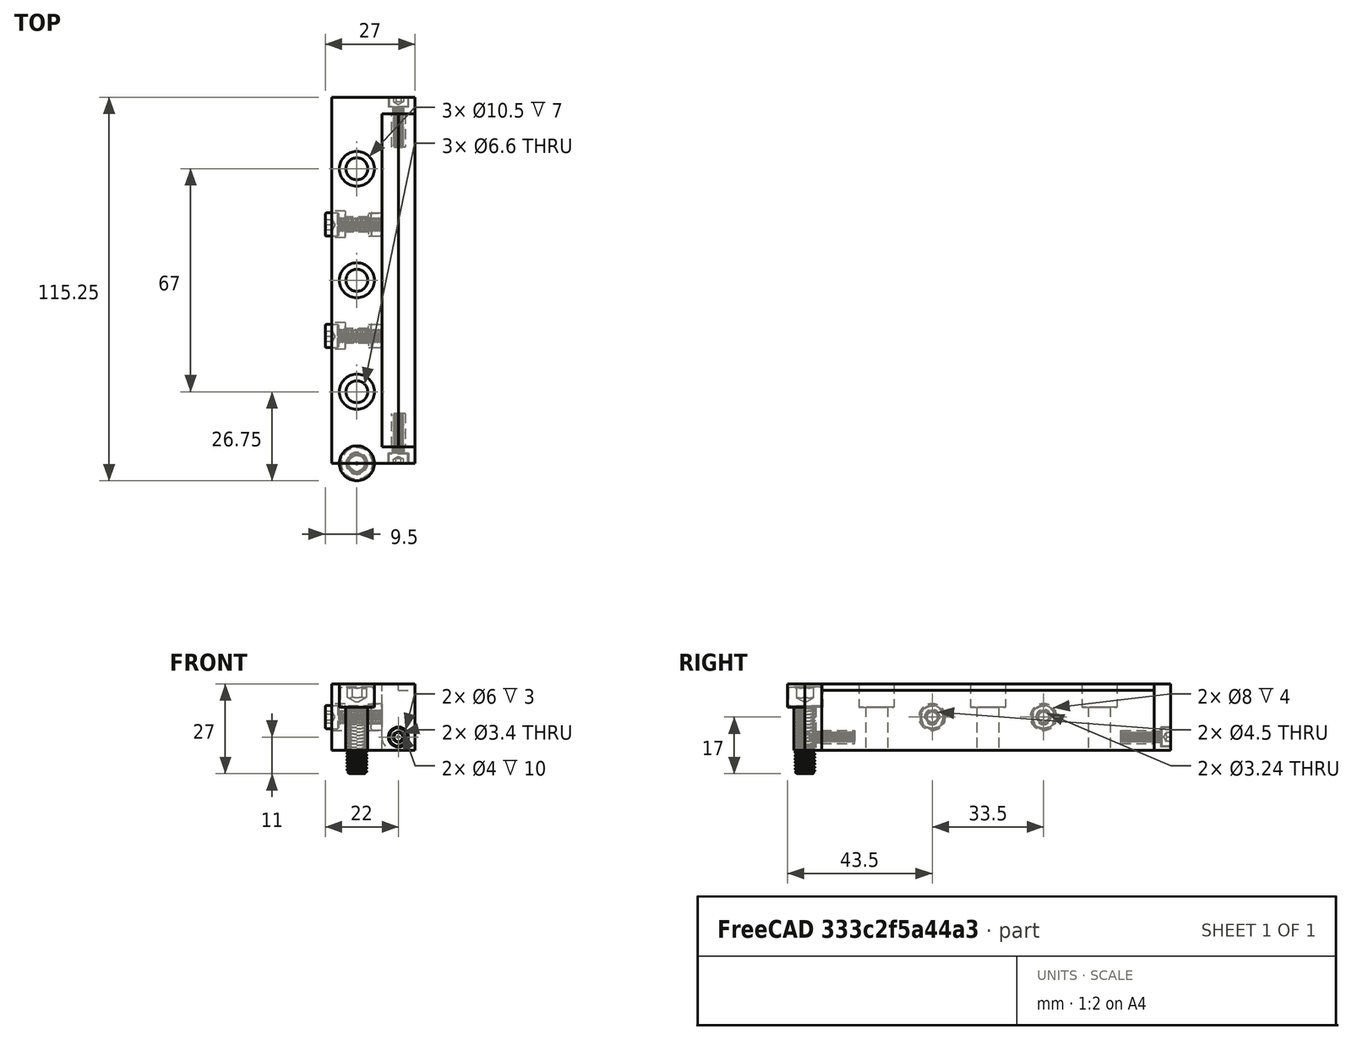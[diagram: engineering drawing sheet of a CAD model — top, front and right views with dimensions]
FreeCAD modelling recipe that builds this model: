
FCSTD DOCUMENT  (FreeCAD 1.0R1.0rc2)
Label: DeepClampingJaws
License: All rights reserved
LicenseURL: http://en.wikipedia.org/wiki/All_rights_reserved
objects: Part::Cylinder×12, Part::MultiFuse×9, Part::FeaturePython×9, Part::Cut×7, Part::Box×4, Sketcher::SketchObject×2, PartDesign::Pad×2, PartDesign::Body×2, Part::Fillet×2, Spreadsheet::Sheet×1
note: 53 computed .brp shape members not serialized (recipe doc carries the construction recipe); baked Part::Feature solids carry a one-line shape summary decoded from their .brp

FEATURE [Spreadsheet::Sheet] Spreadsheet  label="DeepCalmpParameters"
  cells = A2='Jaw height; B2(jaw_height)=20; A3='Jaw width; B3(jaw_width)=100; A4='Jaw thickness; B4(jaw_thickness)=10; A5='T-Nut spacing; B5(tnutSpacing)=33.5; A6='T-'Nut count; B6(tnutCount)=3; A7='Jawholder thickness side; B7(jawholderThicknessSide)=5; A8='Jawholder thickness; B8(jawholderThickness)=15; A9='Clamp jaw step; B9(jawstepheight)=2
FEATURE [Part::Box] Box  label="ClampBlank"
  AttacherType = Attacher::AttachEngine3D
  Height = 20
  Length = 10
  Placement = pos=(15,5,0) rot=(0,0,1;0rad)
  Width = 100
  expr: .Placement.Base.x = <<DeepCalmpParameters>>.jawholderThickness
  expr: .Placement.Base.y = <<DeepCalmpParameters>>.jawholderThicknessSide
  expr: Height = <<DeepCalmpParameters>>.jaw_height
  expr: Length = <<DeepCalmpParameters>>.jaw_thickness
  expr: Width = <<DeepCalmpParameters>>.jaw_width
FEATURE [Part::Box] Box001  label="Cube001"
  AttacherType = Attacher::AttachEngine3D
  Height = 20
  Length = 25
  Width = 110
  expr: Height = <<DeepCalmpParameters>>.jaw_height
  expr: Length = <<DeepCalmpParameters>>.jaw_thickness + <<DeepCalmpParameters>>.jawholderThickness
  expr: Width = <<DeepCalmpParameters>>.jaw_width + 2 * <<DeepCalmpParameters>>.jawholderThicknessSide
FEATURE [Part::Box] Box002  label="Cube002"
  AttacherType = Attacher::AttachEngine3D
  Height = 20
  Length = 10
  Placement = pos=(15,5,0) rot=(0,0,1;0rad)
  Width = 100
  expr: .Placement.Base.x = <<DeepCalmpParameters>>.jawholderThickness
  expr: .Placement.Base.y = <<DeepCalmpParameters>>.jawholderThicknessSide
  expr: Height = <<DeepCalmpParameters>>.jaw_height
  expr: Length = <<DeepCalmpParameters>>.jaw_thickness
  expr: Width = <<DeepCalmpParameters>>.jaw_width
FEATURE [Part::Cut] Cut
  Base = -> Box001
  Tool = -> Box002
FEATURE [Part::Cylinder] Cylinder
  Angle = 360
  AttacherType = Attacher::AttachEngine3D
  FirstAngle = 0
  Height = 20
  Radius = 3.3
  SecondAngle = 0
  expr: Height = <<DeepCalmpParameters>>.jaw_height
FEATURE [Part::Cylinder] Cylinder001
  Angle = 360
  AttacherType = Attacher::AttachEngine3D
  FirstAngle = 0
  Height = 7
  Placement = pos=(0,0,13) rot=(0,0,1;0rad)
  Radius = 5.25
  SecondAngle = 0
  expr: .Placement.Base.z = <<DeepCalmpParameters>>.jaw_height - 7
FEATURE [Part::MultiFuse] Fusion  label="MountScrewTNut1"
  Placement = pos=(7.5,0,0) rot=(0,0,1;0rad)
  Shapes = -> [Cylinder,Cylinder001]
  expr: .Placement.Base.x = <<DeepCalmpParameters>>.jawholderThickness / 2
  expr: .Placement.Base.y = 0
FEATURE [Part::FeaturePython] Screw001  label="M6x20-Screw"  # Fasteners workbench fastener (typed FeaturePython)
  Placement = pos=(7.5,0,13) rot=(0,0,1;0rad)
  diameter = 7
  invert = false
  leftHanded = false
  length = 14
  lengthCustom = 20
  matchOuter = false
  offset = 0
  thread = true
  type = 48
  expr: .Placement.Base.x = <<DeepCalmpParameters>>.jawholderThickness / 2
  expr: .Placement.Base.y = 0
  expr: .Placement.Base.z = <<DeepCalmpParameters>>.jaw_height - 7
  expr: lengthCustom = <<DeepCalmpParameters>>.jaw_height
FEATURE [Part::FeaturePython] Array  # Draft array (typed FeaturePython)
  AlwaysSyncPlacement = false
  Angle = 360
  ArrayType = 0
  Axis = (0,0,1)
  Base = -> Screw001
  Center = (0,0,0)
  Count = 3
  ExpandArray = false
  Fuse = false
  IntervalAxis = (0,0,0)
  IntervalX = (25,0,0)
  IntervalY = (0,33.5,0)
  IntervalZ = (0,0,100)
  NumberCircles = 3
  NumberPolar = 5
  NumberX = 1
  NumberY = 3
  NumberZ = 1
  Placement = pos=(0,21.5,0) rot=(0,0,1;0rad)
  PlacementList = 3 placements: arithmetic series from (7.5,0,13) step (0,33.5,0) to (7.5,67,13)
  RadialDistance = 50
  ScaleList = (3) [(1,1,1),(1,1,1),(1,1,1)]
  Symmetry = 1
  TangentialDistance = 25
  expr: .IntervalY.y = <<DeepCalmpParameters>>.tnutSpacing
  expr: .Placement.Base.y = <<DeepCalmpParameters>>.jaw_width / 2 + <<DeepCalmpParameters>>.jawholderThicknessSide - (<<DeepCalmpParameters>>.tnutCount - 1) / 2 * <<DeepCalmpParameters>>.tnutSpacing
  expr: NumberY = <<DeepCalmpParameters>>.tnutCount
FEATURE [Part::FeaturePython] Array001  # Draft array (typed FeaturePython)
  AlwaysSyncPlacement = false
  Angle = 360
  ArrayType = 0
  Axis = (0,0,1)
  Base = -> Fusion
  Center = (0,0,0)
  Count = 3
  ExpandArray = false
  Fuse = false
  IntervalAxis = (0,0,0)
  IntervalX = (100,0,0)
  IntervalY = (0,33.5,0)
  IntervalZ = (0,0,100)
  NumberCircles = 3
  NumberPolar = 5
  NumberX = 1
  NumberY = 3
  NumberZ = 1
  Placement = pos=(0,21.5,0) rot=(0,0,1;0rad)
  PlacementList = 3 placements: arithmetic series from (7.5,0,0) step (0,33.5,0) to (7.5,67,0)
  RadialDistance = 50
  ScaleList = (3) [(1,1,1),(1,1,1),(1,1,1)]
  Symmetry = 1
  TangentialDistance = 25
  expr: .IntervalY.y = <<DeepCalmpParameters>>.tnutSpacing
  expr: .Placement.Base.y = <<DeepCalmpParameters>>.jaw_width / 2 + <<DeepCalmpParameters>>.jawholderThicknessSide - (<<DeepCalmpParameters>>.tnutCount - 1) / 2 * <<DeepCalmpParameters>>.tnutSpacing
  expr: NumberY = <<DeepCalmpParameters>>.tnutCount
FEATURE [Part::Cut] Cut001
  Base = -> Cut
  Tool = -> Array001
FEATURE [Part::Box] Box003  label="ClampStep"
  AttacherType = Attacher::AttachEngine3D
  Height = 2
  Length = 5
  Placement = pos=(20,5,18) rot=(0,0,1;0rad)
  Width = 100
  expr: .Placement.Base.x = <<DeepCalmpParameters>>.jawholderThickness + <<DeepCalmpParameters>>.jaw_thickness / 2
  expr: .Placement.Base.y = <<DeepCalmpParameters>>.jawholderThicknessSide
  expr: .Placement.Base.z = <<DeepCalmpParameters>>.jaw_height - <<DeepCalmpParameters>>.jawstepheight
  expr: Height = <<DeepCalmpParameters>>.jawstepheight
  expr: Length = <<DeepCalmpParameters>>.jaw_thickness / 2
  expr: Width = <<DeepCalmpParameters>>.jaw_width
FEATURE [Part::Cut] Cut002
  Base = -> Box
  Tool = -> Box003
FEATURE [Part::Cylinder] Cylinder002  label="M3ThreadHole"
  Angle = 360
  AttacherType = Attacher::AttachEngine3D
  FirstAngle = 0
  Height = 10
  Placement = pos=(20,15,4) rot=(1,0,0;1.5708rad)
  Radius = 2
  SecondAngle = 0
  expr: .Placement.Base.x = <<DeepCalmpParameters>>.jaw_thickness / 2 + <<DeepCalmpParameters>>.jawholderThickness
  expr: .Placement.Base.y = 10 + <<DeepCalmpParameters>>.jawholderThicknessSide
FEATURE [Part::Cylinder] Cylinder003  label="M3ThreadHole001"
  Angle = 360
  AttacherType = Attacher::AttachEngine3D
  FirstAngle = 0
  Height = 10
  Placement = pos=(20,105,4) rot=(1,0,0;1.5708rad)
  Radius = 2
  SecondAngle = 0
  expr: .Placement.Base.x = <<DeepCalmpParameters>>.jaw_thickness / 2 + <<DeepCalmpParameters>>.jawholderThickness
  expr: .Placement.Base.y = <<DeepCalmpParameters>>.jawholderThicknessSide + <<DeepCalmpParameters>>.jaw_width
FEATURE [Part::MultiFuse] Fusion001
  Shapes = -> [Cylinder002,Cylinder003]
FEATURE [Part::Cut] Cut003  label="ClampA"
  Base = -> Cut002
  Tool = -> Fusion001
FEATURE [Part::Cylinder] Cylinder004
  Angle = 360
  AttacherType = Attacher::AttachEngine3D
  FirstAngle = 0
  Height = 3
  Placement = pos=(0,0,12) rot=(0,0,1;0rad)
  Radius = 3
  SecondAngle = 0
  expr: .Placement.Base.z = <<DeepCalmpParameters>>.jawholderThicknessSide + 10 - 3
FEATURE [Part::Cylinder] Cylinder005
  Angle = 360
  AttacherType = Attacher::AttachEngine3D
  FirstAngle = 0
  Height = 15
  Radius = 1.7
  SecondAngle = 0
  expr: Height = <<DeepCalmpParameters>>.jawholderThicknessSide + 10
  expr: Radius = 3.4 / 2
FEATURE [Part::MultiFuse] Fusion002  label="M3ScrewTPL001"
  Placement = pos=(20,15,4) rot=(1,0,0;1.5708rad)
  Shapes = -> [Cylinder004,Cylinder005]
  expr: .Placement.Base.x = <<DeepCalmpParameters>>.jawholderThickness + <<DeepCalmpParameters>>.jaw_thickness / 2
  expr: .Placement.Base.y = <<DeepCalmpParameters>>.jawholderThicknessSide + 10
  expr: .Placement.Base.z = 4
FEATURE [Part::Cylinder] Cylinder006
  Angle = 360
  AttacherType = Attacher::AttachEngine3D
  FirstAngle = 0
  Height = 3
  Placement = pos=(0,0,12) rot=(0,0,1;0rad)
  Radius = 3
  SecondAngle = 0
  expr: .Placement.Base.z = <<DeepCalmpParameters>>.jawholderThicknessSide + 10 - 3
FEATURE [Part::Cylinder] Cylinder007
  Angle = 360
  AttacherType = Attacher::AttachEngine3D
  FirstAngle = 0
  Height = 15
  Radius = 1.7
  SecondAngle = 0
  expr: Height = <<DeepCalmpParameters>>.jawholderThicknessSide + 10
  expr: Radius = 3.4 / 2
FEATURE [Part::MultiFuse] Fusion003  label="M3ScrewTPL002"
  Placement = pos=(20,95,4) rot=(1,0,0;-1.5708rad)
  Shapes = -> [Cylinder006,Cylinder007]
  expr: .Placement.Base.x = <<DeepCalmpParameters>>.jawholderThickness + <<DeepCalmpParameters>>.jaw_thickness / 2
  expr: .Placement.Base.y = <<DeepCalmpParameters>>.jaw_width + 2 * <<DeepCalmpParameters>>.jawholderThicknessSide - (<<DeepCalmpParameters>>.jawholderThicknessSide + 10)
  expr: .Placement.Base.z = 4
FEATURE [Part::MultiFuse] Fusion004
  Shapes = -> [Fusion002,Fusion003]
FEATURE [Part::Cut] Cut004
  Base = -> Cut001
  Tool = -> Fusion004
FEATURE [Part::FeaturePython] Screw  label="M3x12-Screw"  # Fasteners workbench fastener (typed FeaturePython)
  Placement = pos=(20,3,4) rot=(1,0,0;1.5708rad)
  diameter = 4
  invert = false
  leftHanded = false
  length = 10
  lengthCustom = 12
  matchOuter = false
  offset = 0
  thread = true
  type = 48
  expr: .Placement.Base.x = <<DeepCalmpParameters>>.jawholderThickness + <<DeepCalmpParameters>>.jaw_thickness / 2
  expr: lengthCustom = <<DeepCalmpParameters>>.jawholderThicknessSide + 10 - 3
FEATURE [Part::FeaturePython] Screw002  label="M3x12-Screw001"  # Fasteners workbench fastener (typed FeaturePython)
  Placement = pos=(20,107,4) rot=(1,0,0;-1.5708rad)
  diameter = 4
  invert = false
  leftHanded = false
  length = 10
  lengthCustom = 12
  matchOuter = false
  offset = 0
  thread = true
  type = 48
  expr: .Placement.Base.x = <<DeepCalmpParameters>>.jawholderThickness + <<DeepCalmpParameters>>.jaw_thickness / 2
  expr: .Placement.Base.y = -3 + <<DeepCalmpParameters>>.jaw_width + <<DeepCalmpParameters>>.jawholderThicknessSide * 2
  expr: lengthCustom = <<DeepCalmpParameters>>.jawholderThicknessSide + 10 - 3
FEATURE [Part::FeaturePython] Nut  label="M4-Nut"  # Fasteners workbench fastener (typed FeaturePython)
  Placement = pos=(11.8,38.25,10) rot=(0,0.099504,0;1.5708rad)
  diameter = 6
  invert = false
  leftHanded = false
  matchOuter = false
  offset = 0
  thread = false
  type = 25
  expr: .Placement.Base.x = <<DeepCalmpParameters>>.jawholderThickness - 3.2
  expr: .Placement.Base.y = <<DeepCalmpParameters>>.jaw_width / 2 + <<DeepCalmpParameters>>.jawholderThicknessSide - <<DeepCalmpParameters>>.tnutSpacing / 2
  expr: .Placement.Base.z = <<DeepCalmpParameters>>.jaw_height / 2
FEATURE [Part::FeaturePython] Nut001  label="M4-Nut001"  # Fasteners workbench fastener (typed FeaturePython)
  Placement = pos=(11.8,71.75,10) rot=(0,0.099504,0;1.5708rad)
  diameter = 6
  invert = false
  leftHanded = false
  matchOuter = false
  offset = 0
  thread = false
  type = 25
  expr: .Placement.Base.x = <<DeepCalmpParameters>>.jawholderThickness - 3.2
  expr: .Placement.Base.y = <<DeepCalmpParameters>>.jaw_width / 2 + <<DeepCalmpParameters>>.jawholderThicknessSide + <<DeepCalmpParameters>>.tnutSpacing / 2
  expr: .Placement.Base.z = <<DeepCalmpParameters>>.jaw_height / 2
FEATURE [Part::FeaturePython] Screw003  label="M4x13-Screw"  # Fasteners workbench fastener (typed FeaturePython)
  Placement = pos=(2,38.25,10) rot=(0,1,0;-1.5708rad)
  diameter = 5
  invert = false
  leftHanded = false
  length = 11
  lengthCustom = 13
  matchOuter = false
  offset = 0
  thread = true
  type = 48
  expr: .Placement.Base.y = <<DeepCalmpParameters>>.jaw_width / 2 + <<DeepCalmpParameters>>.jawholderThicknessSide - <<DeepCalmpParameters>>.tnutSpacing / 2
  expr: .Placement.Base.z = <<DeepCalmpParameters>>.jaw_height / 2
  expr: lengthCustom = <<DeepCalmpParameters>>.jawholderThickness - 4 + 2
FEATURE [Part::FeaturePython] Screw004  label="M4x13-Screw001"  # Fasteners workbench fastener (typed FeaturePython)
  Placement = pos=(2,71.75,10) rot=(0,1,0;-1.5708rad)
  diameter = 5
  invert = false
  leftHanded = false
  length = 11
  lengthCustom = 13
  matchOuter = false
  offset = 0
  thread = true
  type = 48
  expr: .Placement.Base.y = <<DeepCalmpParameters>>.jaw_width / 2 + <<DeepCalmpParameters>>.jawholderThicknessSide + <<DeepCalmpParameters>>.tnutSpacing / 2
  expr: .Placement.Base.z = <<DeepCalmpParameters>>.jaw_height / 2
  expr: lengthCustom = <<DeepCalmpParameters>>.jawholderThickness - 4 + 2
FEATURE [Part::Cylinder] Cylinder008
  Angle = 360
  AttacherType = Attacher::AttachEngine3D
  FirstAngle = 0
  Height = 4
  Placement = pos=(0,0,0) rot=(0,1,0;1.5708rad)
  Radius = 4
  SecondAngle = 0
FEATURE [Part::Cylinder] Cylinder009
  Angle = 360
  AttacherType = Attacher::AttachEngine3D
  FirstAngle = 0
  Height = 15
  Placement = pos=(0,0,0) rot=(0,1,0;1.5708rad)
  Radius = 2.25
  SecondAngle = 0
  expr: Height = <<DeepCalmpParameters>>.jawholderThickness
FEATURE [Part::MultiFuse] Fusion005  label="M4ScrewTPL001"
  Placement = pos=(0,38.25,10) rot=(0,0,1;0rad)
  Shapes = -> [Cylinder008,Cylinder009]
  expr: .Placement.Base.y = <<DeepCalmpParameters>>.jaw_width / 2 + <<DeepCalmpParameters>>.jawholderThicknessSide - <<DeepCalmpParameters>>.tnutSpacing / 2
  expr: .Placement.Base.z = <<DeepCalmpParameters>>.jaw_height / 2
FEATURE [Part::Cylinder] Cylinder010
  Angle = 360
  AttacherType = Attacher::AttachEngine3D
  FirstAngle = 0
  Height = 4
  Placement = pos=(0,0,0) rot=(0,1,0;1.5708rad)
  Radius = 4
  SecondAngle = 0
FEATURE [Part::Cylinder] Cylinder011
  Angle = 360
  AttacherType = Attacher::AttachEngine3D
  FirstAngle = 0
  Height = 15
  Placement = pos=(0,0,0) rot=(0,1,0;1.5708rad)
  Radius = 2.25
  SecondAngle = 0
  expr: Height = <<DeepCalmpParameters>>.jawholderThickness
FEATURE [Part::MultiFuse] Fusion006  label="M4ScrewTPL002"
  Placement = pos=(0,71.75,10) rot=(0,0,1;0rad)
  Shapes = -> [Cylinder010,Cylinder011]
  expr: .Placement.Base.y = <<DeepCalmpParameters>>.jaw_width / 2 + <<DeepCalmpParameters>>.jawholderThicknessSide + <<DeepCalmpParameters>>.tnutSpacing / 2
  expr: .Placement.Base.z = <<DeepCalmpParameters>>.jaw_height / 2
FEATURE [Part::MultiFuse] Fusion007
  Shapes = -> [Fusion005,Fusion006]
FEATURE [Part::Cut] Cut005
  Base = -> Cut004
  Tool = -> Fusion007
FEATURE [Sketcher::SketchObject] Sketch
  ArcFitTolerance = 1e-06
  AttachmentSupport = -> [XY_Plane]
  FullyConstrained = true
  MakeInternals = false
  MapMode = 5
  sketch-geometry (7):
    g0: LineSegment StartX=4 StartY=0 StartZ=0 EndX=2 EndY=3.4641 EndZ=0
    g1: LineSegment StartX=2 StartY=3.4641 StartZ=0 EndX=-2 EndY=3.4641 EndZ=0
    g2: LineSegment StartX=-2 StartY=3.4641 StartZ=0 EndX=-4 EndY=-2.1214e-12 EndZ=0
    g3: LineSegment StartX=-4 StartY=-2.1214e-12 StartZ=0 EndX=-2 EndY=-3.4641 EndZ=0
    g4: LineSegment StartX=-2 StartY=-3.4641 StartZ=0 EndX=2 EndY=-3.4641 EndZ=0
    g5: LineSegment StartX=2 StartY=-3.4641 StartZ=0 EndX=4 EndY=0 EndZ=0
    g6: Circle [constr] CenterX=0 CenterY=0 CenterZ=0 NormalX=0 NormalY=0 NormalZ=1 AngleXU=0 Radius=4
  constraints (16):
    c: Coincident(g0,g1)
    c: Coincident(g1,g2)
    c: Coincident(g2,g3)
    c: Coincident(g3,g4)
    c: Coincident(g4,g5)
    c: Coincident(g5,g0)
    c: Equal(g0, g1-g5) x5
    c: PointOnObject(g0,g6)
    c: PointOnObject(g1,g6)
    c: PointOnObject(g2,g6)
    c: PointOnObject(g3,g6)
    c: PointOnObject(g4,g6)
    c: PointOnObject(g5,g6)
    c: Radius(g6) = 4
    c: Coincident(g6,g-1)
    c: PointOnObject(g5,g-1)
FEATURE [PartDesign::Pad] Pad
  Direction = (0,0,1)
  Length = 4
  Length2 = 10
  Profile = -> Sketch
  ReferenceAxis = -> Sketch [N_Axis]
  Suppressed = false
  Type = 0
FEATURE [PartDesign::Body] Body  label="DIN934_M4_001"
  AllowCompound = false
  Group = -> [Sketch,Pad]
  Origin = -> Origin
  Placement = pos=(11,38.25,10) rot=(0,1,0;1.5708rad)
  Tip = -> Pad
  expr: .Placement.Base.x = <<DeepCalmpParameters>>.jawholderThickness - 4
  expr: .Placement.Base.y = <<DeepCalmpParameters>>.jaw_width / 2 + <<DeepCalmpParameters>>.jawholderThicknessSide - <<DeepCalmpParameters>>.tnutSpacing / 2
  expr: .Placement.Base.z = <<DeepCalmpParameters>>.jaw_height / 2
FEATURE [Sketcher::SketchObject] Sketch001
  ArcFitTolerance = 1e-06
  AttachmentSupport = -> [XY_Plane001]
  FullyConstrained = true
  MakeInternals = false
  MapMode = 5
  sketch-geometry (7):
    g0: LineSegment StartX=4 StartY=0 StartZ=0 EndX=2 EndY=3.4641 EndZ=0
    g1: LineSegment StartX=2 StartY=3.4641 StartZ=0 EndX=-2 EndY=3.4641 EndZ=0
    g2: LineSegment StartX=-2 StartY=3.4641 StartZ=0 EndX=-4 EndY=-2.1214e-12 EndZ=0
    g3: LineSegment StartX=-4 StartY=-2.1214e-12 StartZ=0 EndX=-2 EndY=-3.4641 EndZ=0
    g4: LineSegment StartX=-2 StartY=-3.4641 StartZ=0 EndX=2 EndY=-3.4641 EndZ=0
    g5: LineSegment StartX=2 StartY=-3.4641 StartZ=0 EndX=4 EndY=0 EndZ=0
    g6: Circle [constr] CenterX=0 CenterY=0 CenterZ=0 NormalX=0 NormalY=0 NormalZ=1 AngleXU=0 Radius=4
  constraints (16):
    c: Coincident(g0,g1)
    c: Coincident(g1,g2)
    c: Coincident(g2,g3)
    c: Coincident(g3,g4)
    c: Coincident(g4,g5)
    c: Coincident(g5,g0)
    c: Equal(g0, g1-g5) x5
    c: PointOnObject(g0,g6)
    c: PointOnObject(g1,g6)
    c: PointOnObject(g2,g6)
    c: PointOnObject(g3,g6)
    c: PointOnObject(g4,g6)
    c: PointOnObject(g5,g6)
    c: Radius(g6) = 4
    c: Coincident(g6,g-1)
    c: PointOnObject(g5,g-1)
FEATURE [PartDesign::Pad] Pad001
  Direction = (0,0,1)
  Length = 4
  Length2 = 10
  Profile = -> Sketch001
  ReferenceAxis = -> Sketch001 [N_Axis]
  Suppressed = false
  Type = 0
FEATURE [PartDesign::Body] Body001  label="DIN934_M4_002"
  AllowCompound = false
  Group = -> [Sketch001,Pad001]
  Origin = -> Origin001
  Placement = pos=(11,71.75,10) rot=(0,1,0;1.5708rad)
  Tip = -> Pad001
  expr: .Placement.Base.x = <<DeepCalmpParameters>>.jawholderThickness - 4
  expr: .Placement.Base.y = <<DeepCalmpParameters>>.jaw_width / 2 + <<DeepCalmpParameters>>.jawholderThicknessSide + <<DeepCalmpParameters>>.tnutSpacing / 2
  expr: .Placement.Base.z = <<DeepCalmpParameters>>.jaw_height / 2
FEATURE [Part::MultiFuse] Fusion008
  Shapes = -> [Body,Body001]
FEATURE [Part::Cut] Cut006  label="VariableChuck"
  Base = -> Cut005
  Tool = -> Fusion008
FEATURE [Part::Fillet] Fillet
  Base = -> Cut003
  EdgeLinks = -> Cut003 [Edge4]
  Edges = 1 edges r=4: [Edge4]
FEATURE [Part::Fillet] Fillet001  label="ClampWithRounding"
  Base = -> Fillet
  EdgeLinks = -> Fillet [Edge21]
  Edges = 1 edges r=4: [Edge21]
